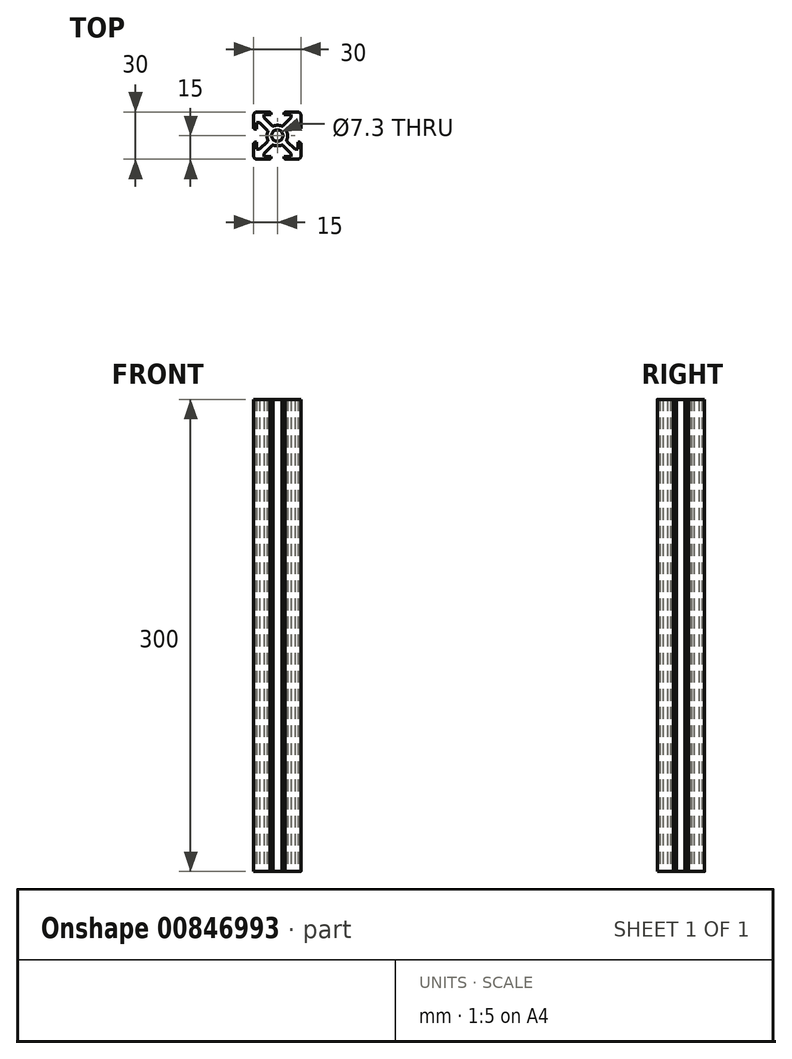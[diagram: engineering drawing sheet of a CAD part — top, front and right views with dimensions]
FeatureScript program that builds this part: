
annotation { "Feature Type Name" : "Feature", "Feature Type Description" : "" }
export const myFeature = defineFeature(function(context is Context, id is Id, definition is map)
    precondition{}
    {
        {
            var Q0;
            Q0=qCreatedBy(makeId("Top.planeOp"),FACE);
            var sketch = newSketch(context, id + "F0", { "sketchPlane" : qUnion([Q0])});
            skLineSegment(sketch, "E0.bottom", {"start": v(2, 0) * mm, "end": v(10.4, 0) * mm});
            skPoint(sketch, "E1.centerSnap0", {"position": v(30, 15) * mm});
            skPoint(sketch, "E2.visualSharp", {"position": v(0, 30) * mm});
            skArc(sketch, "E2.filletArc", {"start": v(2, 30) * mm, "mid": v(0.59, 29.41) * mm, "end": v(0, 28) * mm});
            skPoint(sketch, "E3.visualSharp", {"position": v(0, 0) * mm});
            skArc(sketch, "E3.filletArc", {"start": v(0, 2) * mm, "mid": v(0.59, 0.59) * mm, "end": v(2, 0) * mm});
            skPoint(sketch, "E4.visualSharp", {"position": v(30, 0) * mm});
            skPoint(sketch, "E5.visualSharp", {"position": v(30, 30) * mm});
            skPoint(sketch, "E4.filletArc.start.orphan", {"position": v(28, 0) * mm});
            skLineSegment(sketch, "E6.MirrorCS", {"start": v(29.5, 19) * mm, "end": v(28.3, 19) * mm});
            skArc(sketch, "E7.MirrorCS", {"start": v(21.3, 11.3) * mm, "mid": v(21.08, 11.63) * mm, "end": v(21, 12.01) * mm});
            skLineSegment(sketch, "E8.MirrorCS", {"start": v(30, 10.2) * mm, "end": v(29.5, 10.2) * mm});
            skArc(sketch, "E9.MirrorCS", {"start": v(21, 17.59) * mm, "mid": v(21.08, 17.97) * mm, "end": v(21.3, 18.3) * mm});
            skLineSegment(sketch, "E10.MirrorCS", {"start": v(29.5, 10.8) * mm, "end": v(29.5, 10.2) * mm});
            skLineSegment(sketch, "E11.MirrorCS", {"start": v(30, 19.6) * mm, "end": v(29.5, 19.6) * mm});
            skLineSegment(sketch, "E12.MirrorCS", {"start": v(29.5, 19) * mm, "end": v(29.5, 19.6) * mm});
            skLineSegment(sketch, "E13.MirrorCS", {"start": v(26.3, 6.3) * mm, "end": v(28.3, 6.3) * mm});
            skLineSegment(sketch, "E14.MirrorCS", {"start": v(28.3, 10.8) * mm, "end": v(29.5, 10.8) * mm});
            skLineSegment(sketch, "E15.MirrorCS", {"start": v(28.3, 23.3) * mm, "end": v(26.3, 23.3) * mm});
            skArc(sketch, "E16.MirrorCS", {"start": v(30, 2) * mm, "mid": v(29.41, 0.59) * mm, "end": v(28, 0) * mm});
            skArc(sketch, "E17.MirrorCS", {"start": v(28, 30) * mm, "mid": v(29.41, 29.41) * mm, "end": v(30, 28) * mm});
            skLineSegment(sketch, "E18.MirrorCS", {"start": v(28.3, 6.3) * mm, "end": v(28.3, 10.8) * mm});
            skPoint(sketch, "E19.MirrorP", {"position": v(21, 11.6) * mm});
            skLineSegment(sketch, "E20.MirrorCS", {"start": v(30, 19.6) * mm, "end": v(30, 28) * mm});
            skLineSegment(sketch, "E21.MirrorCS", {"start": v(28.3, 19) * mm, "end": v(28.3, 23.3) * mm});
            skLineSegment(sketch, "E22.MirrorCS", {"start": v(30, 2) * mm, "end": v(30, 10.2) * mm});
            skLineSegment(sketch, "E23.MirrorCS", {"start": v(28, 0) * mm, "end": v(19.2, 0) * mm});
            skArc(sketch, "E24.MirrorCS", {"start": v(21, 17.59) * mm, "mid": v(21.55, 14.8) * mm, "end": v(21, 12.01) * mm});
            skPoint(sketch, "E25.MirrorP", {"position": v(21, 18) * mm});
            skPoint(sketch, "E26.MirrorP", {"position": v(30, 10.8) * mm});
            skLineSegment(sketch, "E27.MirrorCS", {"start": v(26.3, 23.3) * mm, "end": v(21.3, 18.3) * mm});
            skLineSegment(sketch, "E28.MirrorCS", {"start": v(21.3, 11.3) * mm, "end": v(26.3, 6.3) * mm});
            skPoint(sketch, "E29.MirrorP", {"position": v(15, 30) * mm});
            skPoint(sketch, "E30.1.0", {"position": v(12, 21) * mm});
            skLineSegment(sketch, "E30.1.1", {"start": v(23.7, 26.3) * mm, "end": v(23.7, 28.3) * mm});
            skLineSegment(sketch, "E30.1.2", {"start": v(10.4, 30) * mm, "end": v(2, 30) * mm});
            skLineSegment(sketch, "E30.1.3", {"start": v(18.7, 21.3) * mm, "end": v(23.7, 26.3) * mm});
            skLineSegment(sketch, "E30.1.4", {"start": v(23.7, 28.3) * mm, "end": v(19.2, 28.3) * mm});
            skArc(sketch, "E30.1.5", {"start": v(12.41, 21) * mm, "mid": v(15.2, 21.55) * mm, "end": v(17.99, 21) * mm});
            skPoint(sketch, "E30.1.6", {"position": v(19.2, 30) * mm});
            skLineSegment(sketch, "E30.1.8", {"start": v(11, 28.3) * mm, "end": v(6.7, 28.3) * mm});
            skLineSegment(sketch, "E30.1.9", {"start": v(6.7, 26.3) * mm, "end": v(11.7, 21.3) * mm});
            skLineSegment(sketch, "E30.1.10", {"start": v(28, 30) * mm, "end": v(19.8, 30) * mm});
            skPoint(sketch, "E30.1.11", {"position": v(18.4, 21) * mm});
            skLineSegment(sketch, "E30.1.12", {"start": v(6.7, 28.3) * mm, "end": v(6.7, 26.3) * mm});
            skLineSegment(sketch, "E30.1.13", {"start": v(19.2, 28.3) * mm, "end": v(19.2, 29.5) * mm});
            skLineSegment(sketch, "E30.1.14", {"start": v(11, 29.5) * mm, "end": v(10.4, 29.5) * mm});
            skLineSegment(sketch, "E30.1.15", {"start": v(10.4, 30) * mm, "end": v(10.4, 29.5) * mm});
            skLineSegment(sketch, "E30.1.16", {"start": v(11, 29.5) * mm, "end": v(11, 28.3) * mm});
            skLineSegment(sketch, "E30.1.17", {"start": v(19.2, 29.5) * mm, "end": v(19.8, 29.5) * mm});
            skArc(sketch, "E30.1.18", {"start": v(18.7, 21.3) * mm, "mid": v(18.37, 21.08) * mm, "end": v(17.99, 21) * mm});
            skArc(sketch, "E30.1.19", {"start": v(12.41, 21) * mm, "mid": v(12.03, 21.08) * mm, "end": v(11.7, 21.3) * mm});
            skLineSegment(sketch, "E30.1.20", {"start": v(19.8, 30) * mm, "end": v(19.8, 29.5) * mm});
            skPoint(sketch, "E30.2.21", {"position": v(15, 0) * mm});
            skPoint(sketch, "E30.2.22", {"position": v(15, 0) * mm});
            skPoint(sketch, "E30.center", {"position": v(15, 15) * mm});
            skLineSegment(sketch, "E30.anchor1", {"start": v(15, 15) * mm, "end": v(14.25, 14.8) * mm, "construction": true});
            skLineSegment(sketch, "E30.anchor2", {"start": v(15, 15) * mm, "end": v(15.75, 15.2) * mm, "construction": true});
            skLineSegment(sketch, "E31", {"start": v(0, 28) * mm, "end": v(0, 19.6) * mm});
            skLineSegment(sketch, "E32.MirrorCS", {"start": v(11, 0.5) * mm, "end": v(10.4, 0.5) * mm});
            skLineSegment(sketch, "E33.MirrorCS", {"start": v(19.2, 1.7) * mm, "end": v(19.2, 0.5) * mm});
            skLineSegment(sketch, "E34.MirrorCS", {"start": v(19.2, 0.5) * mm, "end": v(19.8, 0.5) * mm});
            skLineSegment(sketch, "E35.MirrorCS", {"start": v(19.8, 0) * mm, "end": v(19.8, 0.5) * mm});
            skLineSegment(sketch, "E36.MirrorCS", {"start": v(10.4, 0) * mm, "end": v(10.4, 0.5) * mm});
            skLineSegment(sketch, "E37.MirrorCS", {"start": v(11, 0.5) * mm, "end": v(11, 1.7) * mm});
            skLineSegment(sketch, "E38.MirrorCS", {"start": v(23.7, 3.7) * mm, "end": v(23.7, 1.7) * mm});
            skLineSegment(sketch, "E39.MirrorCS", {"start": v(11, 1.7) * mm, "end": v(6.7, 1.7) * mm});
            skLineSegment(sketch, "E40.MirrorCS", {"start": v(23.7, 1.7) * mm, "end": v(19.2, 1.7) * mm});
            skPoint(sketch, "E41.MirrorP", {"position": v(19.2, 0) * mm});
            skLineSegment(sketch, "E42.MirrorCS", {"start": v(6.7, 1.7) * mm, "end": v(6.7, 3.7) * mm});
            skArc(sketch, "E43.MirrorCS", {"start": v(12.41, 9) * mm, "mid": v(12.03, 8.92) * mm, "end": v(11.7, 8.7) * mm});
            skArc(sketch, "E44.MirrorCS", {"start": v(18.7, 8.7) * mm, "mid": v(18.37, 8.92) * mm, "end": v(17.99, 9) * mm});
            skArc(sketch, "E45.MirrorCS", {"start": v(12.41, 9) * mm, "mid": v(15.2, 8.45) * mm, "end": v(17.99, 9) * mm});
            skPoint(sketch, "E46.MirrorP", {"position": v(18.4, 9) * mm});
            skPoint(sketch, "E47.MirrorP", {"position": v(12, 9) * mm});
            skLineSegment(sketch, "E48.MirrorCS", {"start": v(6.7, 3.7) * mm, "end": v(11.7, 8.7) * mm});
            skLineSegment(sketch, "E49.MirrorCS", {"start": v(18.7, 8.7) * mm, "end": v(23.7, 3.7) * mm});
            skArc(sketch, "E50.MirrorCS", {"start": v(8.7, 11.3) * mm, "mid": v(8.92, 11.63) * mm, "end": v(9, 12.01) * mm});
            skArc(sketch, "E51.MirrorCS", {"start": v(9, 17.59) * mm, "mid": v(8.45, 14.8) * mm, "end": v(9, 12.01) * mm});
            skArc(sketch, "E52.MirrorCS", {"start": v(9, 17.59) * mm, "mid": v(8.92, 17.97) * mm, "end": v(8.7, 18.3) * mm});
            skLineSegment(sketch, "E53.MirrorCS", {"start": v(1.7, 23.3) * mm, "end": v(3.7, 23.3) * mm});
            skLineSegment(sketch, "E54.MirrorCS", {"start": v(0.5, 19) * mm, "end": v(0.5, 19.6) * mm});
            skLineSegment(sketch, "E55.MirrorCS", {"start": v(1.7, 19) * mm, "end": v(1.7, 23.3) * mm});
            skLineSegment(sketch, "E56.MirrorCS", {"start": v(0.5, 19) * mm, "end": v(1.7, 19) * mm});
            skLineSegment(sketch, "E57.MirrorCS", {"start": v(0, 19.6) * mm, "end": v(0.5, 19.6) * mm});
            skLineSegment(sketch, "E58.MirrorCS", {"start": v(0, 10.2) * mm, "end": v(0.5, 10.2) * mm});
            skLineSegment(sketch, "E59.MirrorCS", {"start": v(1.7, 10.8) * mm, "end": v(0.5, 10.8) * mm});
            skLineSegment(sketch, "E60.MirrorCS", {"start": v(0.5, 10.8) * mm, "end": v(0.5, 10.2) * mm});
            skLineSegment(sketch, "E61.MirrorCS", {"start": v(3.7, 6.3) * mm, "end": v(1.7, 6.3) * mm});
            skLineSegment(sketch, "E62.MirrorCS", {"start": v(8.7, 11.3) * mm, "end": v(3.7, 6.3) * mm});
            skLineSegment(sketch, "E63.MirrorCS", {"start": v(0, 2) * mm, "end": v(0, 10.2) * mm});
            skLineSegment(sketch, "E64.MirrorCS", {"start": v(1.7, 6.3) * mm, "end": v(1.7, 10.8) * mm});
            skPoint(sketch, "E65.MirrorP", {"position": v(0, 10.8) * mm});
            skLineSegment(sketch, "E66.MirrorCS", {"start": v(3.7, 23.3) * mm, "end": v(8.7, 18.3) * mm});
            skPoint(sketch, "E67.orphan", {"position": v(11.35, 15) * mm});
            skPoint(sketch, "E68.end.orphan", {"position": v(18.65, 15) * mm});
            skLineSegment(sketch, "E69.trimOffspring", {"start": v(0, 10.8) * mm, "end": v(0, 2) * mm});
            skSolve(sketch);
        }
        {
            var Q0;
            Q0=makeQuery(id+"F0.imprint","IMPRINT",FACE,{"disambiguationData":[TD([[makeQuery(id+"F0.imprint","IMPRINT",EDGE,{"derivedFrom":sQuery(id+"F0.wireOp",EDGE,"E0.bottom")}),1.0]])]});
            extrude(context, id + "F1", {"entities" : qUnion([Q0]), "depth" : 300 * mm, "offsetDistance" : 25 * mm});
        }
        {
            var Q0;
            Q0=makeQuery(id+"F1.opExtrude","CAP_FACE",FACE,{"disambiguationData":[OSD([sQuery(id+"F0.wireOp",EDGE,"E0.bottom"),sQuery(id+"F0.wireOp",EDGE,"E2.filletArc"),sQuery(id+"F0.wireOp",EDGE,"E3.filletArc"),sQuery(id+"F0.wireOp",EDGE,"E6.MirrorCS"),sQuery(id+"F0.wireOp",EDGE,"E7.MirrorCS"),sQuery(id+"F0.wireOp",EDGE,"E8.MirrorCS"),sQuery(id+"F0.wireOp",EDGE,"E9.MirrorCS"),sQuery(id+"F0.wireOp",EDGE,"E10.MirrorCS"),sQuery(id+"F0.wireOp",EDGE,"E11.MirrorCS"),sQuery(id+"F0.wireOp",EDGE,"E12.MirrorCS"),sQuery(id+"F0.wireOp",EDGE,"E13.MirrorCS"),sQuery(id+"F0.wireOp",EDGE,"E14.MirrorCS"),sQuery(id+"F0.wireOp",EDGE,"E15.MirrorCS"),sQuery(id+"F0.wireOp",EDGE,"E16.MirrorCS"),sQuery(id+"F0.wireOp",EDGE,"E17.MirrorCS"),sQuery(id+"F0.wireOp",EDGE,"E18.MirrorCS"),sQuery(id+"F0.wireOp",EDGE,"E20.MirrorCS"),sQuery(id+"F0.wireOp",EDGE,"E21.MirrorCS"),sQuery(id+"F0.wireOp",EDGE,"E22.MirrorCS"),sQuery(id+"F0.wireOp",EDGE,"E23.MirrorCS"),sQuery(id+"F0.wireOp",EDGE,"E24.MirrorCS"),sQuery(id+"F0.wireOp",EDGE,"E27.MirrorCS"),sQuery(id+"F0.wireOp",EDGE,"E28.MirrorCS"),sQuery(id+"F0.wireOp",EDGE,"E30.1.1"),sQuery(id+"F0.wireOp",EDGE,"E30.1.2"),sQuery(id+"F0.wireOp",EDGE,"E30.1.3"),sQuery(id+"F0.wireOp",EDGE,"E30.1.4"),sQuery(id+"F0.wireOp",EDGE,"E30.1.5"),sQuery(id+"F0.wireOp",EDGE,"E30.1.8"),sQuery(id+"F0.wireOp",EDGE,"E30.1.9"),sQuery(id+"F0.wireOp",EDGE,"E30.1.10"),sQuery(id+"F0.wireOp",EDGE,"E30.1.12"),sQuery(id+"F0.wireOp",EDGE,"E30.1.13"),sQuery(id+"F0.wireOp",EDGE,"E30.1.14"),sQuery(id+"F0.wireOp",EDGE,"E30.1.15"),sQuery(id+"F0.wireOp",EDGE,"E30.1.16"),sQuery(id+"F0.wireOp",EDGE,"E30.1.17"),sQuery(id+"F0.wireOp",EDGE,"E30.1.18"),sQuery(id+"F0.wireOp",EDGE,"E30.1.19"),sQuery(id+"F0.wireOp",EDGE,"E30.1.20"),sQuery(id+"F0.wireOp",EDGE,"E31"),sQuery(id+"F0.wireOp",EDGE,"E32.MirrorCS"),sQuery(id+"F0.wireOp",EDGE,"E33.MirrorCS"),sQuery(id+"F0.wireOp",EDGE,"E34.MirrorCS"),sQuery(id+"F0.wireOp",EDGE,"E35.MirrorCS"),sQuery(id+"F0.wireOp",EDGE,"E36.MirrorCS"),sQuery(id+"F0.wireOp",EDGE,"E37.MirrorCS"),sQuery(id+"F0.wireOp",EDGE,"E38.MirrorCS"),sQuery(id+"F0.wireOp",EDGE,"E39.MirrorCS"),sQuery(id+"F0.wireOp",EDGE,"E40.MirrorCS"),sQuery(id+"F0.wireOp",EDGE,"E42.MirrorCS"),sQuery(id+"F0.wireOp",EDGE,"E48.MirrorCS"),sQuery(id+"F0.wireOp",EDGE,"E49.MirrorCS"),sQuery(id+"F0.wireOp",EDGE,"E44.MirrorCS"),sQuery(id+"F0.wireOp",EDGE,"E43.MirrorCS"),sQuery(id+"F0.wireOp",EDGE,"E45.MirrorCS"),sQuery(id+"F0.wireOp",EDGE,"E50.MirrorCS"),sQuery(id+"F0.wireOp",EDGE,"E51.MirrorCS"),sQuery(id+"F0.wireOp",EDGE,"E52.MirrorCS"),sQuery(id+"F0.wireOp",EDGE,"E53.MirrorCS"),sQuery(id+"F0.wireOp",EDGE,"E54.MirrorCS"),sQuery(id+"F0.wireOp",EDGE,"E55.MirrorCS"),sQuery(id+"F0.wireOp",EDGE,"E56.MirrorCS"),sQuery(id+"F0.wireOp",EDGE,"E57.MirrorCS"),sQuery(id+"F0.wireOp",EDGE,"E58.MirrorCS"),sQuery(id+"F0.wireOp",EDGE,"E59.MirrorCS"),sQuery(id+"F0.wireOp",EDGE,"E60.MirrorCS"),sQuery(id+"F0.wireOp",EDGE,"E61.MirrorCS"),sQuery(id+"F0.wireOp",EDGE,"E62.MirrorCS"),sQuery(id+"F0.wireOp",EDGE,"E64.MirrorCS"),sQuery(id+"F0.wireOp",EDGE,"E66.MirrorCS"),sQuery(id+"F0.wireOp",EDGE,"E69.trimOffspring")])],"isStart":false});
            var sketch = newSketch(context, id + "F2", { "sketchPlane" : qUnion([Q0])});
            skCircle(sketch, "E70", {"center": v(15, 15) * mm, "radius": 3.65 * mm});
            skSolve(sketch);
        }
        {
            var Q0;
            Q0=makeQuery(id+"F2.imprint","IMPRINT",FACE,{"disambiguationData":[TD([[makeQuery(id+"F2.imprint","IMPRINT",EDGE,{"derivedFrom":sQuery(id+"F2.wireOp",EDGE,"E70")}),1.0]])]});
            var Q1;
            Q1=sQuery(id+"F2.wireOp",EDGE,"E70");
            extrude(context, id + "F3", {"entities" : qUnion([Q0]), "operationType" : NewBodyOperationType.REMOVE, "surfaceEntities" : qUnion([Q1]), "oppositeDirection" : true, "depth" : 300 * mm, "offsetDistance" : 25 * mm});
        }
    });
